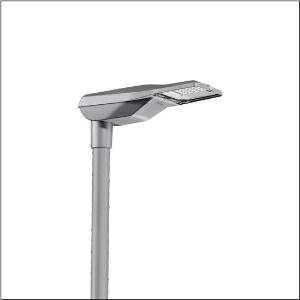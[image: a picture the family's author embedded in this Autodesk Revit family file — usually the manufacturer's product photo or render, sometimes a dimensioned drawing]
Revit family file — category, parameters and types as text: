
# Revit family: streetlight_sl_21_iq_micro___stw1_0a_5xe1e41g08cb_8385
name_source: partatom
category: Lighting Fixtures
units: mm (PartAtom-declared; Revit-internal decimal feet)

## family parameters
Cut with Voids When Loaded = No
Host = Face
Light Source = No
Part Type = Normal
Room Calculation Point = No
Round Connector Dimension = Use Diameter
Shared = No

## types (1)
- --- (1 x LED, 2980 lm, 19.4 W, 4000K)
    Apparent Load = 19 VA
    CIE Flux Codes = 38 75 98 100 100
    Color Rendering = 70
    Color Temperature = 4000K
    Default Elevation = 1800 mm
    Description = Streetlight SL 21 iQ micro, mast luminaire, primary light control with lens, of PMMA, primary optical cover: cover, of toughened safety glass, transparent, light distribution: STW1.0a, light emission: direct distribution, primary light characteristic: asymmetric, installation type: post-top, side-entry, LED, High Power LED, rated luminous flux: 2.980lm, luminous efficacy: 154lm/W, light colour: 740, colour temperature: 4000K, control: Street-Remote, Auto-Match, Temp-Guard, Lumen-Switch, Night-Set, Smart-Wire, Light-Fading, Desk-Remote (wireless, voltage-free reading and setting of iQ features in the workshop via application-optimized NFC function/RFID function), optimised constant luminous flux control (CLO 2.0), presetting dimming linear, mains connection: 220..240V, AC, 50/60Hz, start of lifetime: 19W, end of service life: 20W, reduction: 10W, luminaire housing, of diecast aluminium, powder-coated, Siteco® metallic grey (DB 702S), corrosivity category C5 mid according to DIN EN ISO 12944, please order mast flange separately, inclination adjustable: 0°, 5°, 10°, 15°, sealing non-destructively replaceable, multi-level sealing system, length: 528mm, width: 235mm, height: 110mm, mast flange for spigot size: 42mm (side-entry): 5XC10008XM4, 60/48mm (side-entry/post-top): 5XC10108XM2, 76/60mm (side-entry/post-top): 5XC10108XM1, protection rating (complete): IP66, insulation class (complete): insulation class II (safety insulation), certification: CE, ENEC, ENEC+, VDE, impact resistance: IK09, permissible operating ambient temperature for outdoor applications: -40..+50°C, standard-compliant lighting for roads and squares, packaging unit: 1 piece

Light Distribution: STW1.0a
    Height = 110 mm
    Lamp = 1 x LED
    Lamp Light Flux = 2980 lm
    Lamp Power = 19.4 W
    Lamp count = 1
    Length = 528 mm
    Luminous efficacy = 154 lm/W
    Manufacturer = Siteco
    ModVariant = No
    Model = 5XE1E41G08CB
    Number of Poles = 1
    OnlyDefault = Yes
    Power Factor = 1
    Product Name = Streetlight SL 21 iQ micro | STW1.0a
    Product group = mast luminaire | pylon top
    ProductGroupID = 6100
    Protection Class = Protection class II
    Protection Degree = IP 66
    RLX_Detail_Level = 1
    RLX_Emergency_Light_Flux = 0 lm
    RLX_Emergency_Type = 0
    RLX_Emergency_Type_DB = No
    RlxData = <blob elided: 98597 chars, md5=1533da58>
    Socket = socket
    Standby Power = 0 W
    System Light Flux = 2980 lm
    System Power = 19 W
    Type Comments = factory setting: luminous flux: 100 % | dim-lin: 254 | 387 mA
    Type Image = l_1006881.jpg
    URL = http://relux.com
    VarID = @adj_070113
    Voltage = 0 V
    Weight = 0.00 kg
    Width = 235 mm

## geometry (parser evidence)
native form markers: Blend x4, Sweep x10
no freeform markers — native parametric forms only
